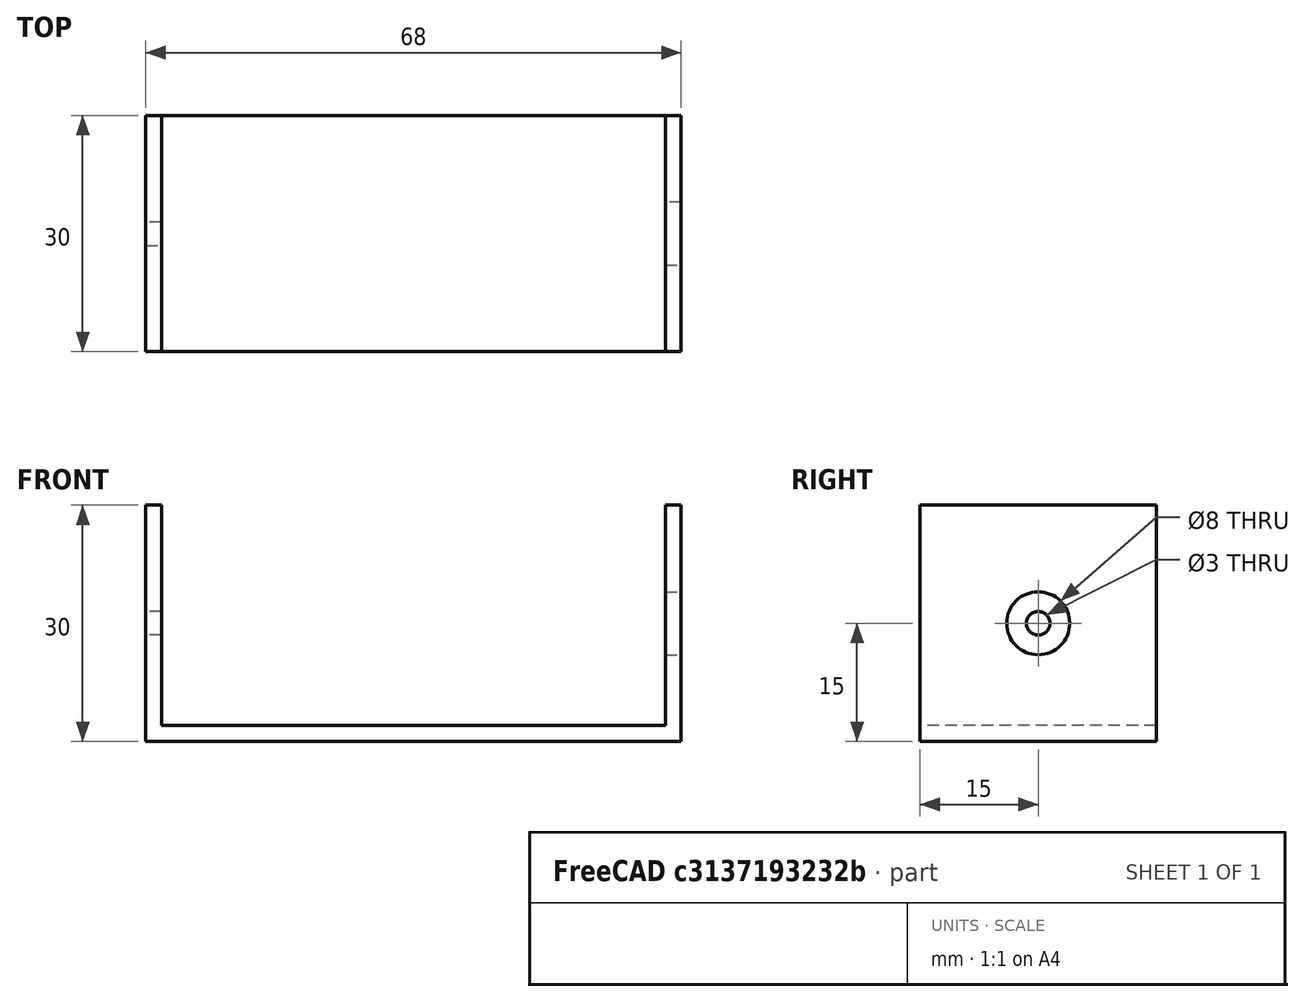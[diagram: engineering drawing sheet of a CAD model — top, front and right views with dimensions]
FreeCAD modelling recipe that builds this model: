
FCSTD DOCUMENT  (FreeCAD 0.20RUnknown)
Label: camera_hold
License: All rights reserved
LicenseURL: http://en.wikipedia.org/wiki/All_rights_reserved
objects: Sketcher::SketchObject×5, PartDesign::Pocket×3, PartDesign::Pad×1, PartDesign::Body×1, PartDesign::Fillet×1, Mesh::Feature×1
note: 16 computed .brp shape members not serialized (recipe doc carries the construction recipe); baked Part::Feature solids carry a one-line shape summary decoded from their .brp

FEATURE [Sketcher::SketchObject] Sketch
  FullyConstrained = true
  MapMode = 5
  Support = -> [XY_Plane]
  sketch-geometry (4):
    g0: LineSegment StartX=-34 StartY=15 StartZ=0 EndX=34 EndY=15 EndZ=0
    g1: LineSegment StartX=34 StartY=15 StartZ=0 EndX=34 EndY=-15 EndZ=0
    g2: LineSegment StartX=34 StartY=-15 StartZ=0 EndX=-34 EndY=-15 EndZ=0
    g3: LineSegment StartX=-34 StartY=-15 StartZ=0 EndX=-34 EndY=15 EndZ=0
  constraints (10):
    c: Coincident(g0,g1)
    c: Coincident(g1,g2)
    c: Coincident(g2,g3)
    c: Coincident(g3,g0)
    c: Horizontal(g2)
    c: Vertical(g1)
    c: Symmetric(g0,g0,g-2)
    c: Symmetric(g0,g2,g-1)
    c: Distance(g0) = 68
    c: Distance(g3) = 30
FEATURE [PartDesign::Pad] Pad
  Direction = (0,0,1)
  Length = 30
  Length2 = 10
  Profile = -> Sketch
  ReferenceAxis = -> Sketch [N_Axis]
  Type = 0
FEATURE [Sketcher::SketchObject] Sketch001
  FullyConstrained = true
  MapMode = 5
  Placement = pos=(0,0,30) rot=(0,0,1;0rad)
  Support = -> [Pad]
  sketch-geometry (4):
    g0: LineSegment StartX=-32 StartY=15 StartZ=0 EndX=32 EndY=15 EndZ=0
    g1: LineSegment StartX=32 StartY=15 StartZ=0 EndX=32 EndY=-15 EndZ=0
    g2: LineSegment StartX=32 StartY=-15 StartZ=0 EndX=-32 EndY=-15 EndZ=0
    g3: LineSegment StartX=-32 StartY=-15 StartZ=0 EndX=-32 EndY=15 EndZ=0
  constraints (10):
    c: Coincident(g0,g1)
    c: Coincident(g1,g2)
    c: Coincident(g2,g3)
    c: Coincident(g3,g0)
    c: Horizontal(g2)
    c: Vertical(g1)
    c: Symmetric(g0,g0,g-2)
    c: Symmetric(g0,g2,g-1)
    c: Distance(g0) = 64
    c: Distance(g3) = 30
FEATURE [PartDesign::Pocket] Pocket
  BaseFeature = -> Pad
  Direction = (0,0,-1)
  Length = 28
  Length2 = 5
  Profile = -> Sketch001
  ReferenceAxis = -> Sketch001 [N_Axis]
  Type = 0
FEATURE [Sketcher::SketchObject] Sketch002
  FullyConstrained = true
  MapMode = 5
  Placement = pos=(34,0,0) rot=(0.57735,0.57735,0.57735;2.0944rad)
  Support = -> [Pocket]
  sketch-geometry (1):
    g0: Circle CenterX=0 CenterY=15 CenterZ=0 NormalX=0 NormalY=0 NormalZ=1 AngleXU=0 Radius=4
  constraints (3):
    c: PointOnObject(g0,g-2)
    c: Distance(g-1,g0) = 15
    c: Diameter(g0) = 8
FEATURE [PartDesign::Pocket] Pocket001
  BaseFeature = -> Pocket
  Direction = (-1,0,0)
  Length = 2
  Length2 = 5
  Profile = -> Sketch002
  ReferenceAxis = -> Sketch002 [N_Axis]
  Type = 0
FEATURE [Sketcher::SketchObject] Sketch003
  FullyConstrained = true
  MapMode = 5
  Placement = pos=(-34,0,0) rot=(0.57735,-0.57735,-0.57735;2.0944rad)
  Support = -> [Pocket001]
  sketch-geometry (1):
    g0: Circle CenterX=0 CenterY=15 CenterZ=0 NormalX=0 NormalY=0 NormalZ=1 AngleXU=0 Radius=1.5
  constraints (3):
    c: PointOnObject(g0,g-2)
    c: DistanceY(g-1,g0) = 15
    c: Diameter(g0) = 3
FEATURE [PartDesign::Pocket] Pocket002
  BaseFeature = -> Pocket001
  Direction = (1,0,0)
  Length = 2
  Length2 = 5
  Profile = -> Sketch003
  ReferenceAxis = -> Sketch003 [N_Axis]
  Type = 0
FEATURE [Sketcher::SketchObject] Sketch004
  FullyConstrained = true
  MapMode = 5
  Placement = pos=(34,0,0) rot=(0.57735,0.57735,0.57735;2.0944rad)
  Support = -> [Pocket002]
FEATURE [PartDesign::Body] Body
  Group = -> [Sketch,Pad,Sketch001,Pocket,Sketch002,Pocket001,Sketch003,Pocket002,Sketch004]
  Origin = -> Origin
  Tip = -> Pocket002
FEATURE [PartDesign::Fillet] Fillet
  Base = -> Pocket002 [Face3]
  BaseFeature = -> Pocket002
  Radius = 1
  SupportTransform = false
  UseAllEdges = false
FEATURE [Mesh::Feature] Mesh  label="Body (Meshed)"
